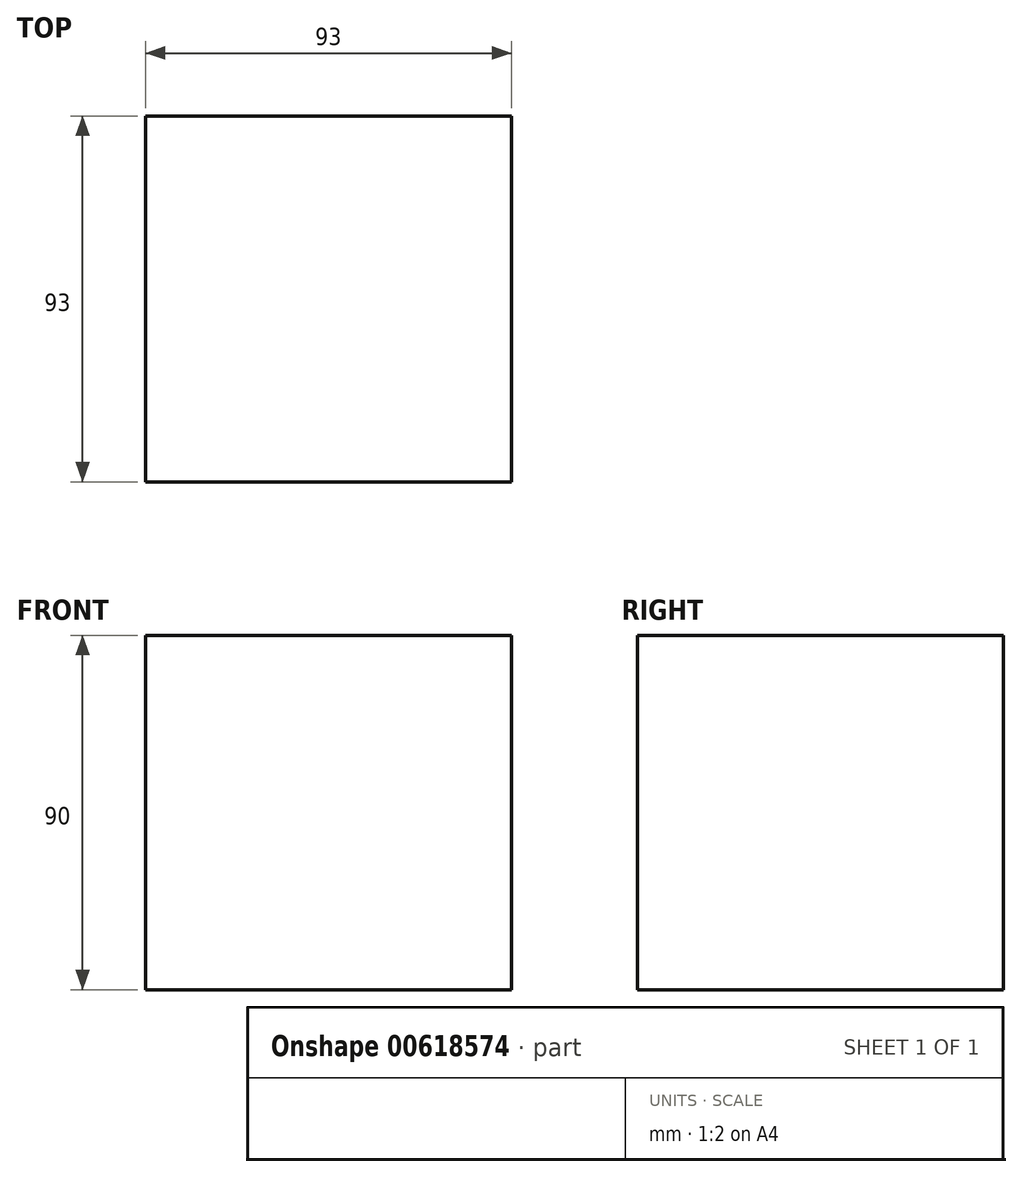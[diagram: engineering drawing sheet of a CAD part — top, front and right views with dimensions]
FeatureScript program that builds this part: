
annotation { "Feature Type Name" : "Feature", "Feature Type Description" : "" }
export const myFeature = defineFeature(function(context is Context, id is Id, definition is map)
    precondition{}
    {
        {
            var Q0;
            Q0=qCreatedBy(makeId("Top.planeOp"),FACE);
            var sketch = newSketch(context, id + "F0", { "sketchPlane" : qUnion([Q0])});
            skLineSegment(sketch, "E0.bottom", {"start": v(0, 0) * mm, "end": v(93, 0) * mm});
            skLineSegment(sketch, "E0.top", {"start": v(0, 93) * mm, "end": v(93, 93) * mm});
            skLineSegment(sketch, "E0.left", {"start": v(0, 0) * mm, "end": v(0, 93) * mm});
            skLineSegment(sketch, "E0.right", {"start": v(93, 0) * mm, "end": v(93, 93) * mm});
            skSolve(sketch);
        }
        {
            var Q0;
            Q0=qSketchRegion(id+"F0",true);
            extrude(context, id + "F1", {"entities" : qUnion([Q0]), "depth" : 90 * mm, "offsetDistance" : 25.4 * mm});
        }
        {
            var Q0;
            Q0=makeQuery(id+"F1.opExtrude","CAP_FACE",FACE,{"disambiguationData":[OSD([sQuery(id+"F0.wireOp",EDGE,"E0.bottom"),sQuery(id+"F0.wireOp",EDGE,"E0.top"),sQuery(id+"F0.wireOp",EDGE,"E0.left"),sQuery(id+"F0.wireOp",EDGE,"E0.right")])],"isStart":false});
            var sketch = newSketch(context, id + "F2", { "sketchPlane" : qUnion([Q0])});
            skLineSegment(sketch, "E1.bottom", {"start": v(7.62, 50.84) * mm, "end": v(84.62, 50.84) * mm});
            skLineSegment(sketch, "E1.top", {"start": v(7.62, 42.84) * mm, "end": v(84.62, 42.84) * mm});
            skLineSegment(sketch, "E1.left", {"start": v(7.62, 50.84) * mm, "end": v(7.62, 42.84) * mm});
            skLineSegment(sketch, "E1.right", {"start": v(84.62, 50.84) * mm, "end": v(84.62, 42.84) * mm});
            skSolve(sketch);
        }
        {
            var Q0;
            Q0=sQuery(id+"F2.wireOp",EDGE,"E1.left");
            var Q1;
            Q1=sQuery(id+"F2.wireOp",EDGE,"E1.bottom");
            var Q2;
            Q2=sQuery(id+"F2.wireOp",EDGE,"E1.right");
            var Q3;
            Q3=sQuery(id+"F2.wireOp",EDGE,"E1.top");
            extrude(context, id + "F3", {"bodyType" : ToolBodyType.SURFACE, "surfaceEntities" : qUnion([Q0, Q1, Q2, Q3]), "oppositeDirection" : true, "depth" : 5.08 * mm, "offsetDistance" : 25.4 * mm});
        }
    });
